# Revit family: 95 BELLA VISTA HEAVY BI FOLD.rfa))))
name_source: partatom
category: Generic Models
revit_build: Autodesk Revit 2018 (Build: 20170223_1515(x64)
units: mm (PartAtom-declared; Revit-internal decimal feet)

## family parameters
Always vertical = Yes
Can host rebar = No
Cut with Voids When Loaded = No
Part Type = Normal
Room Calculation Point = No
Round Connector Dimension = Use Diameter
Shared = No
Work Plane-Based = No

## types (1)
- 95 BELLA VISTA HEAVY BI FOLD.rfa))))
    95 BELLA VISTA HEAVY BLADE = <By Category>
    ANGLE = 45.00°
    BI FOLD ANGLE = 45.00°
    BI FOLD DOOR ONE, AND FOUR REMAINDER = 14 mm  [stored 0.0459318 ft]
    BI FOLD DOOR PANEL (LENGTH) ONE, AND FOUR = 736 mm  [stored 2.4147 ft]
    BI FOLD DOOR PANEL (LENGTH) TWO, AND THREE = 750 mm  [stored 2.46063 ft]
    BOTTOM HUNG = <By Category>
    DRIVE ARM = <By Category>
    END CAP = <By Category>
    FRAMING = <By Category>
    HEIGHT = 2200 mm  [stored 7.21785 ft]
    HINGE = <By Category>
    L1 = 739 mm
    LENGTH PIVOT POINT = 11 mm  [stored 0.0360892 ft]
    LOUVRE ANGLE = 45.00°
    PIVOT POINT = 87 mm
    PIVOT POINT REMAINDER = 124 mm
    RAIL LENGTH = 2985 mm
    RAIL LENGTH REMAINDER = 29 mm  [stored 0.0951444 ft]
    SPACING = 90 mm  [stored 0.295276 ft]
    TOP HUNG = <By Category>
    WIDTH = 1132 mm

note: [stored X ft] marks values corroborated as IEEE doubles in the binary element streams (Revit-internal decimal feet)

## geometry (parser evidence)
native form markers: Sweep x45
no freeform markers — native parametric forms only
